# Revit family: DC_Rheem_PLM_Raypak_B0280HWT
name_source: partatom
category: Mechanical Equipment
units: mm (PartAtom-declared; Revit-internal decimal feet)

## family parameters
Cut with Voids When Loaded = No
Host = Face
Part Type = Normal
Room Calculation Point = No
Round Connector Dimension = Use Radius
Shared = No

## types (4) — shared parameters
Basae2 Dist_ANZRS = 105 mm
Base Width_ANZRS = 50 mm  [stored 0.164042 ft]
Base1 Dist_ANZRS = 30 mm
Box HEight_ANZRS = 985 mm
Cold Water Conn. Dist_ANZRS = 215 mm
Cold Water Inlet Diameter_ANZRS = 40 mm
Cold Water Inlet Radius_ANZRS = 20 mm
Conn Height_ANZRS = 700 mm
Gas Conn. Dist_ANZRS = 105 mm
Gas Inlet Height_ANZRS = 370 mm
H1_ANZRS = 940 mm
Height_ANZRS = 1715 mm  [stored 5.62664 ft]
Hot Water Conn. Dist_ANZRS = 170 mm
Hot Water Outlet Diameter_ANZRS = 40 mm
Hot Water outlet radius_ANZRS = 20 mm
Length_ANZRS = 675 mm  [stored 2.21457 ft]
Manufacturer = Raypak
Material_ANZRS = Raypak - Grey Powder Coated Steel
PRV Dist_ANZRS = 210 mm  [stored 0.688976 ft]
PRV_ANZRS = 10 mm  [stored 0.0328084 ft]
Top Dia_ANZRS = 205 mm  [stored 0.672572 ft]
URL = http://www.rheem.com.au
Width_ANZRS = 570 mm  [stored 1.87008 ft]
zero-valued in all types: Default Elevation

## per-type parameters (varying)
| type | Description | Gas Inlet Diameter_ANZRS | Gas Inlet radius_ANZRS | Model | Type Comments |
| Raypak - Gas Water Heater- Outdoor - 278 MJ/h  Natural gas, modulating gas control | Raypak - Gas Water Heater- Outdoor - 278 MJ/h  Natural gas, modulating gas control | 25 mm  [stored 0.082021 ft] | 13 mm | B0280NCM/HWT | Recovery 1061L/h @ 50oC rise |
| Raypak - Gas Water Heater- Outdoor - 278 MJ/h  Natural gas, On/Off gas control | Raypak - Gas Water Heater- Outdoor - 278 MJ/h  Natural gas, On/Off gas control | 20 mm | 10 mm  [stored 0.0328084 ft] | B0280NCO/HWT | Recovery 1061L/h @ 50oC rise |
| Raypak - Gas Water Heater- Outdoor - 261 MJ/h  Propane gas, modulating gas control | Raypak - Gas Water Heater- Outdoor - 261 MJ/h  Propane gas, modulating gas control | 20 mm | 10 mm  [stored 0.0328084 ft] | B0280PCM/HWT | Recovery 998L/h @ 50oC rise |
| Raypak - Gas Water Heater- Outdoor - 261 MJ/h  Propane gas, On/Off gas control | Raypak - Gas Water Heater- Outdoor - 261 MJ/h  Propane gas, modulating gas control | 20 mm | 10 mm  [stored 0.0328084 ft] | B0280PCO/HWT | Recovery 998L/h @ 50oC rise |

note: [stored X ft] marks values corroborated as IEEE doubles in the binary element streams (Revit-internal decimal feet)

## geometry (parser evidence)
native form markers: Blend x10, Sweep x2
no freeform markers — native parametric forms only
